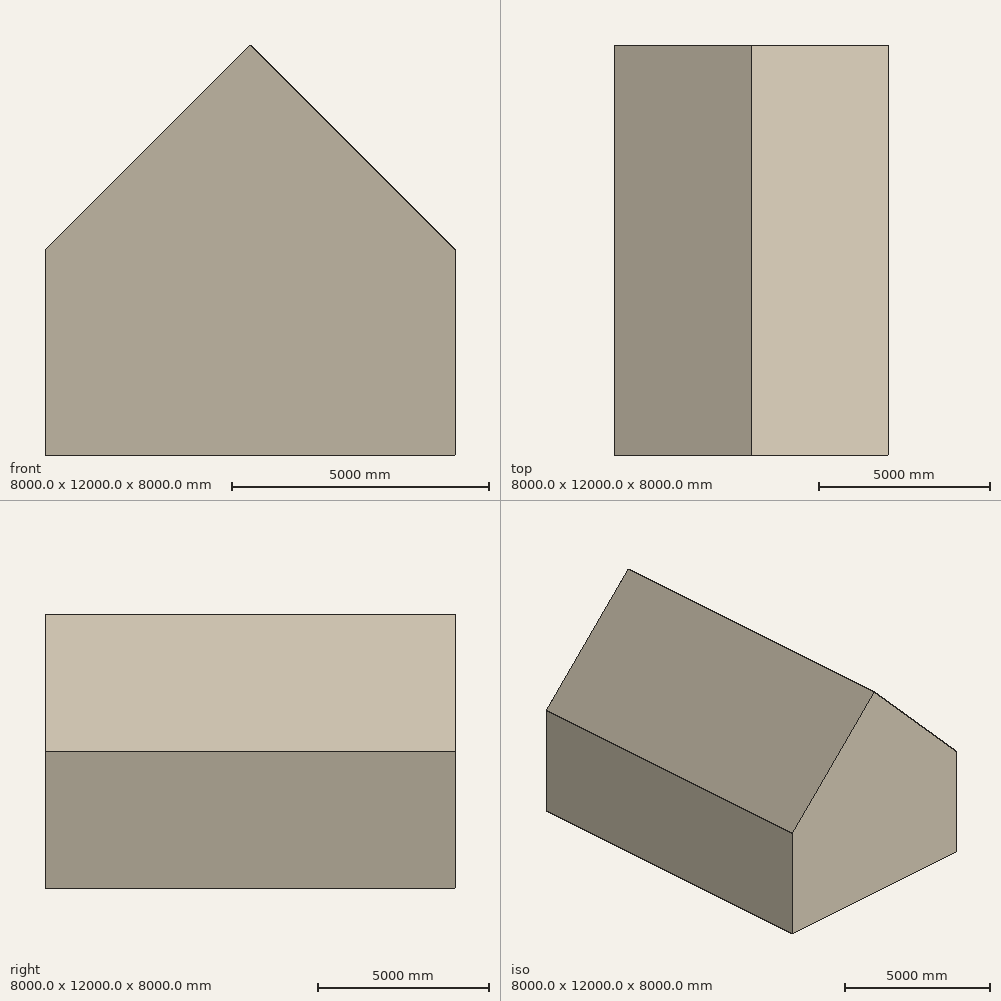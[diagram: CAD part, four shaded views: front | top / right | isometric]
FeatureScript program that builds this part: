
annotation { "Feature Type Name" : "Feature", "Feature Type Description" : "" }
export const myFeature = defineFeature(function(context is Context, id is Id, definition is map)
    precondition{}
    {
        {
            var Q0;
            Q0=qCreatedBy(makeId("Front.planeOp"),FACE);
            var sketch = newSketch(context, id + "F0", { "sketchPlane" : qUnion([Q0])});
            skLineSegment(sketch, "E0", {"start": v(0, 0) * mm, "end": v(8000, 0) * mm});
            skLineSegment(sketch, "E1", {"start": v(0, 0) * mm, "end": v(0, 4000) * mm});
            skLineSegment(sketch, "E2", {"start": v(8000, 0) * mm, "end": v(8000, 4000) * mm});
            skLineSegment(sketch, "E3", {"start": v(0, 4000) * mm, "end": v(4000, 8000) * mm});
            skLineSegment(sketch, "E4", {"start": v(4000, 8000) * mm, "end": v(8000, 4000) * mm});
            skSolve(sketch);
        }
        {
            var Q0;
            Q0=makeQuery(id+"F0.imprint","IMPRINT",FACE,{"disambiguationData":[TD([[makeQuery(id+"F0.imprint","IMPRINT",EDGE,{"derivedFrom":sQuery(id+"F0.wireOp",EDGE,"E0")}),1.0]])]});
            extrude(context, id + "F1", {"entities" : qUnion([Q0]), "depth" : 12000 * mm});
        }
    });
